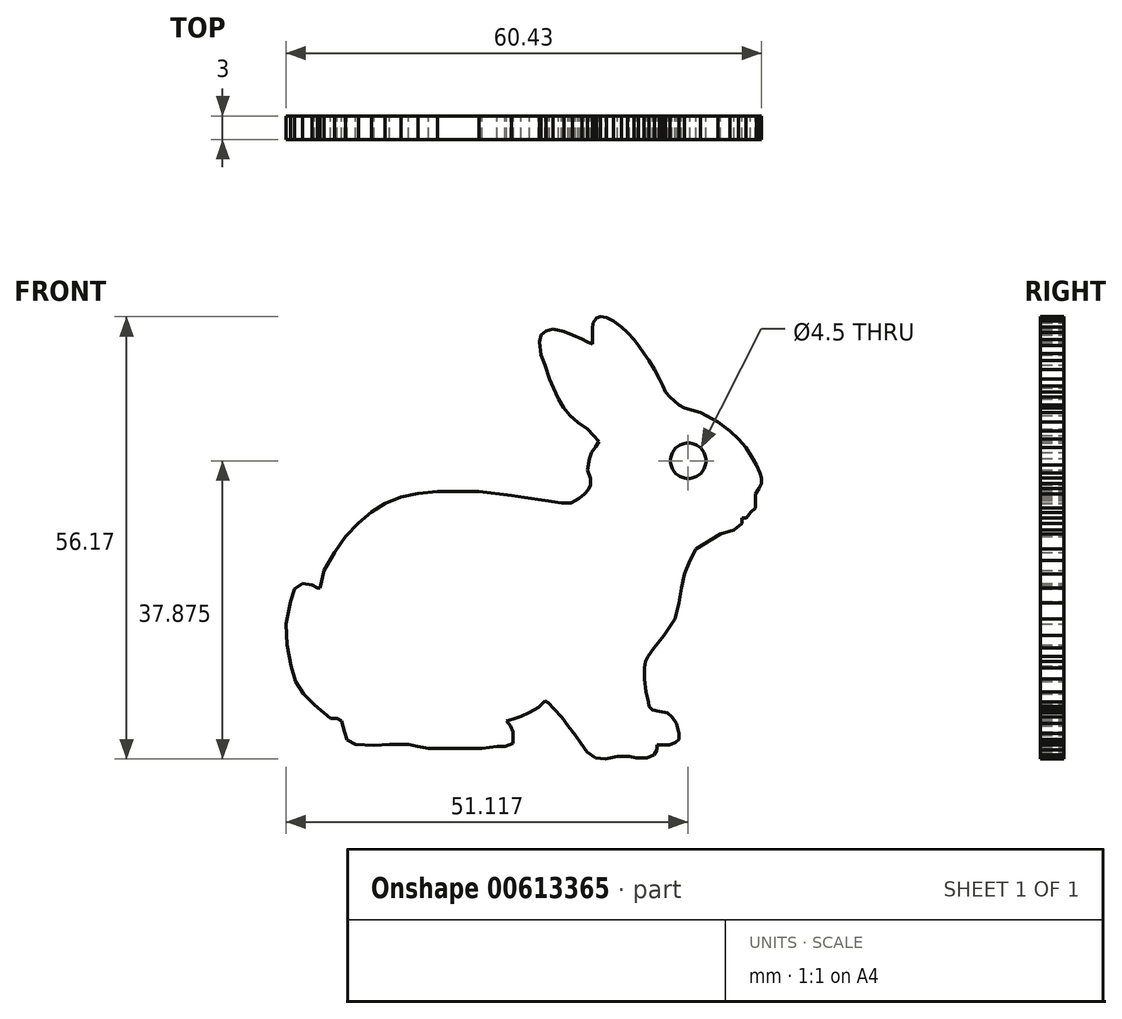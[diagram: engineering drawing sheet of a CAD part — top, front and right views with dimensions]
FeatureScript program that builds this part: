
annotation { "Feature Type Name" : "Feature", "Feature Type Description" : "" }
export const myFeature = defineFeature(function(context is Context, id is Id, definition is map)
    precondition{}
    {
        {
            var Q0;
            Q0=qCreatedBy(makeId("Front.planeOp"),FACE);
            var sketch = newSketch(context, id + "F0", { "sketchPlane" : qUnion([Q0])});
            skLineSegment(sketch, "E0", {"start": v(59.18, 31.9) * mm, "end": v(59.18, 31.2) * mm});
            skLineSegment(sketch, "E1", {"start": v(59.18, 31.2) * mm, "end": v(58.21, 30.37) * mm});
            skLineSegment(sketch, "E2", {"start": v(58.21, 30.37) * mm, "end": v(56.46, 29.85) * mm});
            skLineSegment(sketch, "E3", {"start": v(56.46, 29.85) * mm, "end": v(53.36, 27.96) * mm});
            skLineSegment(sketch, "E4", {"start": v(53.36, 27.96) * mm, "end": v(52.57, 26.52) * mm});
            skLineSegment(sketch, "E5", {"start": v(52.57, 26.52) * mm, "end": v(51.91, 24.8) * mm});
            skLineSegment(sketch, "E6", {"start": v(51.91, 24.8) * mm, "end": v(51.53, 22.99) * mm});
            skLineSegment(sketch, "E7", {"start": v(51.53, 22.99) * mm, "end": v(51.19, 21.11) * mm});
            skLineSegment(sketch, "E8", {"start": v(51.19, 21.11) * mm, "end": v(50.68, 19.1) * mm});
            skLineSegment(sketch, "E9", {"start": v(50.68, 19.1) * mm, "end": v(49.32, 17.01) * mm});
            skLineSegment(sketch, "E10", {"start": v(49.32, 17.01) * mm, "end": v(48.02, 15.39) * mm});
            skLineSegment(sketch, "E11", {"start": v(48.02, 15.39) * mm, "end": v(47.24, 14.33) * mm});
            skLineSegment(sketch, "E12", {"start": v(47.24, 14.33) * mm, "end": v(46.93, 13.71) * mm});
            skLineSegment(sketch, "E13", {"start": v(46.93, 13.71) * mm, "end": v(46.8, 12.88) * mm});
            skLineSegment(sketch, "E14", {"start": v(46.8, 12.88) * mm, "end": v(46.8, 11.49) * mm});
            skLineSegment(sketch, "E15", {"start": v(46.8, 11.49) * mm, "end": v(47.02, 9.82) * mm});
            skLineSegment(sketch, "E16", {"start": v(47.02, 9.82) * mm, "end": v(47.3, 8.54) * mm});
            skLineSegment(sketch, "E17", {"start": v(47.3, 8.54) * mm, "end": v(47.4, 8) * mm});
            skLineSegment(sketch, "E18", {"start": v(47.4, 8) * mm, "end": v(47.8, 7.53) * mm});
            skLineSegment(sketch, "E19", {"start": v(47.8, 7.53) * mm, "end": v(48.73, 7.33) * mm});
            skLineSegment(sketch, "E20", {"start": v(48.73, 7.33) * mm, "end": v(49.72, 7.17) * mm});
            skLineSegment(sketch, "E21", {"start": v(49.72, 7.17) * mm, "end": v(50.33, 6.61) * mm});
            skLineSegment(sketch, "E22", {"start": v(50.33, 6.61) * mm, "end": v(50.85, 5.82) * mm});
            skLineSegment(sketch, "E23", {"start": v(50.85, 5.82) * mm, "end": v(51.16, 4.55) * mm});
            skLineSegment(sketch, "E24", {"start": v(51.16, 4.55) * mm, "end": v(51.16, 3.77) * mm});
            skLineSegment(sketch, "E25", {"start": v(51.16, 3.77) * mm, "end": v(50.77, 3.37) * mm});
            skLineSegment(sketch, "E26", {"start": v(50.77, 3.37) * mm, "end": v(49.97, 3.1) * mm});
            skLineSegment(sketch, "E27", {"start": v(49.97, 3.1) * mm, "end": v(48.4, 3.1) * mm});
            skLineSegment(sketch, "E28", {"start": v(48.4, 3.1) * mm, "end": v(48.4, 2.43) * mm});
            skLineSegment(sketch, "E29", {"start": v(48.4, 2.43) * mm, "end": v(48.04, 1.82) * mm});
            skLineSegment(sketch, "E30", {"start": v(48.04, 1.82) * mm, "end": v(47.14, 1.41) * mm});
            skLineSegment(sketch, "E31", {"start": v(47.14, 1.41) * mm, "end": v(45.74, 1.41) * mm});
            skLineSegment(sketch, "E32", {"start": v(45.74, 1.41) * mm, "end": v(44.91, 1.62) * mm});
            skLineSegment(sketch, "E33", {"start": v(44.91, 1.62) * mm, "end": v(43.35, 1.62) * mm});
            skLineSegment(sketch, "E34", {"start": v(43.35, 1.62) * mm, "end": v(41.85, 1.3) * mm});
            skLineSegment(sketch, "E35", {"start": v(41.85, 1.3) * mm, "end": v(40.56, 1.41) * mm});
            skLineSegment(sketch, "E36", {"start": v(40.56, 1.41) * mm, "end": v(39.54, 2.2) * mm});
            skLineSegment(sketch, "E37", {"start": v(39.54, 2.2) * mm, "end": v(38.77, 3.29) * mm});
            skLineSegment(sketch, "E38", {"start": v(38.77, 3.29) * mm, "end": v(38.07, 4.3) * mm});
            skLineSegment(sketch, "E39", {"start": v(38.07, 4.3) * mm, "end": v(37.07, 5.46) * mm});
            skLineSegment(sketch, "E40", {"start": v(37.07, 5.46) * mm, "end": v(36.3, 6.57) * mm});
            skLineSegment(sketch, "E41", {"start": v(36.3, 6.57) * mm, "end": v(35.28, 7.7) * mm});
            skLineSegment(sketch, "E42", {"start": v(35.28, 7.7) * mm, "end": v(34.6, 8.39) * mm});
            skLineSegment(sketch, "E43", {"start": v(34.6, 8.39) * mm, "end": v(34.18, 8.68) * mm});
            skLineSegment(sketch, "E44", {"start": v(34.18, 8.68) * mm, "end": v(33.34, 7.84) * mm});
            skLineSegment(sketch, "E45", {"start": v(33.34, 7.84) * mm, "end": v(32.19, 7.18) * mm});
            skLineSegment(sketch, "E46", {"start": v(32.19, 7.18) * mm, "end": v(31.1, 6.72) * mm});
            skLineSegment(sketch, "E47", {"start": v(31.1, 6.72) * mm, "end": v(30.18, 6.39) * mm});
            skLineSegment(sketch, "E48", {"start": v(30.18, 6.39) * mm, "end": v(29.26, 6.12) * mm});
            skLineSegment(sketch, "E49", {"start": v(29.26, 6.12) * mm, "end": v(29.8, 5.51) * mm});
            skLineSegment(sketch, "E50", {"start": v(29.8, 5.51) * mm, "end": v(30.13, 4.73) * mm});
            skLineSegment(sketch, "E51", {"start": v(30.13, 4.73) * mm, "end": v(30.13, 4.07) * mm});
            skLineSegment(sketch, "E52", {"start": v(30.13, 4.07) * mm, "end": v(30.13, 3.51) * mm});
            skLineSegment(sketch, "E53", {"start": v(30.13, 3.51) * mm, "end": v(30.13, 3.29) * mm});
            skLineSegment(sketch, "E54", {"start": v(30.13, 3.29) * mm, "end": v(29.07, 2.88) * mm});
            skLineSegment(sketch, "E55", {"start": v(29.07, 2.88) * mm, "end": v(28.07, 2.88) * mm});
            skLineSegment(sketch, "E56", {"start": v(28.07, 2.88) * mm, "end": v(26.19, 2.66) * mm});
            skLineSegment(sketch, "E57", {"start": v(26.19, 2.66) * mm, "end": v(23.74, 2.66) * mm});
            skLineSegment(sketch, "E58", {"start": v(23.74, 2.66) * mm, "end": v(21.88, 2.66) * mm});
            skLineSegment(sketch, "E59", {"start": v(21.88, 2.66) * mm, "end": v(19.4, 2.66) * mm});
            skLineSegment(sketch, "E60", {"start": v(19.4, 2.66) * mm, "end": v(18, 2.88) * mm});
            skLineSegment(sketch, "E61", {"start": v(18, 2.88) * mm, "end": v(16.82, 3.14) * mm});
            skLineSegment(sketch, "E62", {"start": v(16.82, 3.14) * mm, "end": v(14.45, 3.14) * mm});
            skLineSegment(sketch, "E63", {"start": v(14.45, 3.14) * mm, "end": v(12.45, 3) * mm});
            skLineSegment(sketch, "E64", {"start": v(12.45, 3) * mm, "end": v(10.14, 3.13) * mm});
            skLineSegment(sketch, "E65", {"start": v(10.14, 3.13) * mm, "end": v(9.06, 3.73) * mm});
            skLineSegment(sketch, "E66", {"start": v(9.06, 3.73) * mm, "end": v(8.7, 4.73) * mm});
            skLineSegment(sketch, "E67", {"start": v(8.7, 4.73) * mm, "end": v(8.3, 6.14) * mm});
            skLineSegment(sketch, "E68", {"start": v(8.3, 6.14) * mm, "end": v(7.74, 6.47) * mm});
            skLineSegment(sketch, "E69", {"start": v(7.74, 6.47) * mm, "end": v(6.93, 6.47) * mm});
            skLineSegment(sketch, "E70", {"start": v(6.93, 6.47) * mm, "end": v(4.9, 8.14) * mm});
            skLineSegment(sketch, "E71", {"start": v(4.9, 8.14) * mm, "end": v(3.53, 9.54) * mm});
            skLineSegment(sketch, "E72", {"start": v(3.53, 9.54) * mm, "end": v(2.47, 11.15) * mm});
            skLineSegment(sketch, "E73", {"start": v(2.47, 11.15) * mm, "end": v(1.9, 13.14) * mm});
            skLineSegment(sketch, "E74", {"start": v(1.9, 13.14) * mm, "end": v(1.4, 15.75) * mm});
            skLineSegment(sketch, "E75", {"start": v(1.4, 15.75) * mm, "end": v(1.25, 18.43) * mm});
            skLineSegment(sketch, "E76", {"start": v(1.25, 18.43) * mm, "end": v(1.86, 21.3) * mm});
            skLineSegment(sketch, "E77", {"start": v(1.86, 21.3) * mm, "end": v(2.39, 22.87) * mm});
            skLineSegment(sketch, "E78", {"start": v(2.39, 22.87) * mm, "end": v(3.37, 23.56) * mm});
            skLineSegment(sketch, "E79", {"start": v(3.37, 23.56) * mm, "end": v(4.55, 23.4) * mm});
            skLineSegment(sketch, "E80", {"start": v(4.55, 23.4) * mm, "end": v(5.28, 22.99) * mm});
            skLineSegment(sketch, "E81", {"start": v(5.28, 22.99) * mm, "end": v(5.63, 22.99) * mm});
            skLineSegment(sketch, "E82", {"start": v(5.63, 22.99) * mm, "end": v(6.1, 25.22) * mm});
            skLineSegment(sketch, "E83", {"start": v(6.1, 25.22) * mm, "end": v(7.44, 27.53) * mm});
            skLineSegment(sketch, "E84", {"start": v(7.44, 27.53) * mm, "end": v(8.84, 29.53) * mm});
            skLineSegment(sketch, "E85", {"start": v(8.84, 29.53) * mm, "end": v(10.46, 31.27) * mm});
            skLineSegment(sketch, "E86", {"start": v(10.46, 31.27) * mm, "end": v(12.13, 32.66) * mm});
            skLineSegment(sketch, "E87", {"start": v(12.13, 32.66) * mm, "end": v(13.85, 33.74) * mm});
            skLineSegment(sketch, "E88", {"start": v(13.85, 33.74) * mm, "end": v(15.89, 34.56) * mm});
            skLineSegment(sketch, "E89", {"start": v(15.89, 34.56) * mm, "end": v(18.07, 35.02) * mm});
            skLineSegment(sketch, "E90", {"start": v(18.07, 35.02) * mm, "end": v(20.5, 35.25) * mm});
            skLineSegment(sketch, "E91", {"start": v(20.5, 35.25) * mm, "end": v(22.93, 35.25) * mm});
            skLineSegment(sketch, "E92", {"start": v(22.93, 35.25) * mm, "end": v(25.8, 35.25) * mm});
            skLineSegment(sketch, "E93", {"start": v(25.8, 35.25) * mm, "end": v(29.9, 34.74) * mm});
            skLineSegment(sketch, "E94", {"start": v(29.9, 34.74) * mm, "end": v(31.58, 34.5) * mm});
            skLineSegment(sketch, "E95", {"start": v(31.58, 34.5) * mm, "end": v(34.17, 34.11) * mm});
            skLineSegment(sketch, "E96", {"start": v(34.17, 34.11) * mm, "end": v(36.24, 33.84) * mm});
            skLineSegment(sketch, "E97", {"start": v(36.24, 33.84) * mm, "end": v(37.5, 33.84) * mm});
            skLineSegment(sketch, "E98", {"start": v(37.5, 33.84) * mm, "end": v(38.48, 34.41) * mm});
            skLineSegment(sketch, "E99", {"start": v(38.48, 34.41) * mm, "end": v(39.21, 34.95) * mm});
            skLineSegment(sketch, "E100", {"start": v(39.21, 34.95) * mm, "end": v(39.69, 35.51) * mm});
            skLineSegment(sketch, "E101", {"start": v(39.69, 35.51) * mm, "end": v(39.94, 36.1) * mm});
            skLineSegment(sketch, "E102", {"start": v(39.94, 36.1) * mm, "end": v(39.94, 36.93) * mm});
            skLineSegment(sketch, "E103", {"start": v(39.94, 36.93) * mm, "end": v(39.54, 38.02) * mm});
            skLineSegment(sketch, "E104", {"start": v(39.54, 38.02) * mm, "end": v(39.83, 39.44) * mm});
            skLineSegment(sketch, "E105", {"start": v(39.83, 39.44) * mm, "end": v(40.08, 40.2) * mm});
            skLineSegment(sketch, "E106", {"start": v(40.08, 40.2) * mm, "end": v(40.6, 40.94) * mm});
            skLineSegment(sketch, "E107", {"start": v(40.6, 40.94) * mm, "end": v(41, 41.61) * mm});
            skLineSegment(sketch, "E108", {"start": v(41, 41.61) * mm, "end": v(40.3, 42.4) * mm});
            skLineSegment(sketch, "E109", {"start": v(40.3, 42.4) * mm, "end": v(39.57, 43.22) * mm});
            skLineSegment(sketch, "E110", {"start": v(39.57, 43.22) * mm, "end": v(38.4, 44.03) * mm});
            skLineSegment(sketch, "E111", {"start": v(38.4, 44.03) * mm, "end": v(37.38, 44.92) * mm});
            skLineSegment(sketch, "E112", {"start": v(37.38, 44.92) * mm, "end": v(36.53, 45.97) * mm});
            skLineSegment(sketch, "E113", {"start": v(36.53, 45.97) * mm, "end": v(35.9, 47.05) * mm});
            skLineSegment(sketch, "E114", {"start": v(35.9, 47.05) * mm, "end": v(35.26, 48.39) * mm});
            skLineSegment(sketch, "E115", {"start": v(35.26, 48.39) * mm, "end": v(34.77, 49.59) * mm});
            skLineSegment(sketch, "E116", {"start": v(34.77, 49.59) * mm, "end": v(34.17, 51.34) * mm});
            skLineSegment(sketch, "E117", {"start": v(34.17, 51.34) * mm, "end": v(33.68, 52.6) * mm});
            skLineSegment(sketch, "E118", {"start": v(33.68, 52.6) * mm, "end": v(33.5, 54.23) * mm});
            skLineSegment(sketch, "E119", {"start": v(33.5, 54.23) * mm, "end": v(33.67, 55.17) * mm});
            skLineSegment(sketch, "E120", {"start": v(33.67, 55.17) * mm, "end": v(34.28, 55.63) * mm});
            skLineSegment(sketch, "E121", {"start": v(34.28, 55.63) * mm, "end": v(35.19, 55.89) * mm});
            skLineSegment(sketch, "E122", {"start": v(35.19, 55.89) * mm, "end": v(36.57, 55.6) * mm});
            skLineSegment(sketch, "E123", {"start": v(36.57, 55.6) * mm, "end": v(37.7, 55.18) * mm});
            skLineSegment(sketch, "E124", {"start": v(37.7, 55.18) * mm, "end": v(38.87, 54.67) * mm});
            skLineSegment(sketch, "E125", {"start": v(38.87, 54.67) * mm, "end": v(39.6, 54.27) * mm});
            skLineSegment(sketch, "E126", {"start": v(39.6, 54.27) * mm, "end": v(40.2, 53.98) * mm});
            skLineSegment(sketch, "E127", {"start": v(40.2, 53.98) * mm, "end": v(40.2, 55.95) * mm});
            skLineSegment(sketch, "E128", {"start": v(40.2, 55.95) * mm, "end": v(40.3, 56.68) * mm});
            skLineSegment(sketch, "E129", {"start": v(40.3, 56.68) * mm, "end": v(40.7, 57.32) * mm});
            skLineSegment(sketch, "E130", {"start": v(40.7, 57.32) * mm, "end": v(41.2, 57.47) * mm});
            skLineSegment(sketch, "E131", {"start": v(41.2, 57.47) * mm, "end": v(41.98, 57.38) * mm});
            skLineSegment(sketch, "E132", {"start": v(41.98, 57.38) * mm, "end": v(42.9, 56.96) * mm});
            skLineSegment(sketch, "E133", {"start": v(42.9, 56.96) * mm, "end": v(43.88, 56.18) * mm});
            skLineSegment(sketch, "E134", {"start": v(43.88, 56.18) * mm, "end": v(44.66, 55.47) * mm});
            skLineSegment(sketch, "E135", {"start": v(44.66, 55.47) * mm, "end": v(45.46, 54.57) * mm});
            skLineSegment(sketch, "E136", {"start": v(45.46, 54.57) * mm, "end": v(46.07, 53.8) * mm});
            skLineSegment(sketch, "E137", {"start": v(46.07, 53.8) * mm, "end": v(46.74, 52.83) * mm});
            skLineSegment(sketch, "E138", {"start": v(46.74, 52.83) * mm, "end": v(47.4, 51.92) * mm});
            skLineSegment(sketch, "E139", {"start": v(47.4, 51.92) * mm, "end": v(48.07, 50.76) * mm});
            skLineSegment(sketch, "E140", {"start": v(48.07, 50.76) * mm, "end": v(48.69, 49.58) * mm});
            skLineSegment(sketch, "E141", {"start": v(48.69, 49.58) * mm, "end": v(49.16, 48.64) * mm});
            skLineSegment(sketch, "E142", {"start": v(49.16, 48.64) * mm, "end": v(49.5, 47.92) * mm});
            skLineSegment(sketch, "E143", {"start": v(49.5, 47.92) * mm, "end": v(50.03, 47.25) * mm});
            skLineSegment(sketch, "E144", {"start": v(50.03, 47.25) * mm, "end": v(51.16, 46.28) * mm});
            skLineSegment(sketch, "E145", {"start": v(51.16, 46.28) * mm, "end": v(51.87, 45.89) * mm});
            skLineSegment(sketch, "E146", {"start": v(51.87, 45.89) * mm, "end": v(53.94, 45.3) * mm});
            skLineSegment(sketch, "E147", {"start": v(53.94, 45.3) * mm, "end": v(56.13, 44.1) * mm});
            skLineSegment(sketch, "E148", {"start": v(56.13, 44.1) * mm, "end": v(57.69, 42.96) * mm});
            skLineSegment(sketch, "E149", {"start": v(57.69, 42.96) * mm, "end": v(58.76, 41.92) * mm});
            skLineSegment(sketch, "E150", {"start": v(58.76, 41.92) * mm, "end": v(59.7, 40.84) * mm});
            skLineSegment(sketch, "E151", {"start": v(59.7, 40.84) * mm, "end": v(60.39, 39.73) * mm});
            skLineSegment(sketch, "E152", {"start": v(60.39, 39.73) * mm, "end": v(61.06, 38.64) * mm});
            skLineSegment(sketch, "E153", {"start": v(61.06, 38.64) * mm, "end": v(61.48, 37.65) * mm});
            skLineSegment(sketch, "E154", {"start": v(61.48, 37.65) * mm, "end": v(61.68, 36.96) * mm});
            skLineSegment(sketch, "E155", {"start": v(61.68, 36.96) * mm, "end": v(61.68, 36.3) * mm});
            skLineSegment(sketch, "E156", {"start": v(61.68, 36.3) * mm, "end": v(61.36, 35.64) * mm});
            skLineSegment(sketch, "E157", {"start": v(61.36, 35.64) * mm, "end": v(60.9, 34.95) * mm});
            skLineSegment(sketch, "E158", {"start": v(60.9, 34.95) * mm, "end": v(60.9, 33.94) * mm});
            skLineSegment(sketch, "E159", {"start": v(60.9, 33.94) * mm, "end": v(60.9, 33.16) * mm});
            skLineSegment(sketch, "E160", {"start": v(60.9, 33.16) * mm, "end": v(60.3, 32.6) * mm});
            skLineSegment(sketch, "E161", {"start": v(60.3, 32.6) * mm, "end": v(59.74, 31.88) * mm});
            skLineSegment(sketch, "E162", {"start": v(59.74, 31.88) * mm, "end": v(59.18, 31.9) * mm});
            skCircle(sketch, "E163", {"center": v(52.37, 39.17) * mm, "radius": 2.25 * mm});
            skSolve(sketch);
        }
        {
            var Q0;
            Q0=makeQuery(id+"F0.imprint","IMPRINT",FACE,{"disambiguationData":[TD([[makeQuery(id+"F0.imprint","IMPRINT",EDGE,{"derivedFrom":sQuery(id+"F0.wireOp",EDGE,"E0")}),-1.0]])]});
            extrude(context, id + "F1", {"entities" : qUnion([Q0]), "depth" : 3 * mm, "offsetDistance" : 25 * mm});
        }
    });
